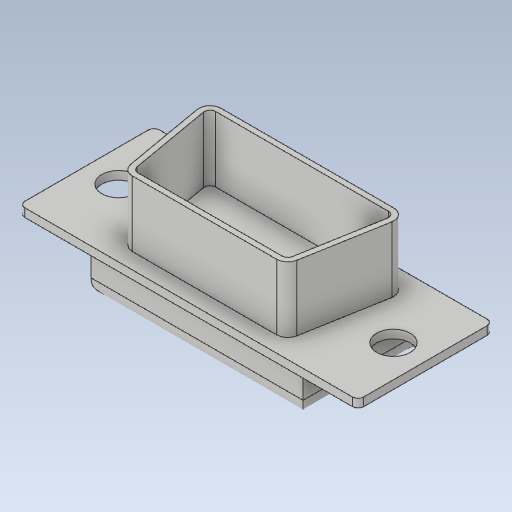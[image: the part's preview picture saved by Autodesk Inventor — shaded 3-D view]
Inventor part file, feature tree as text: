
AUTODESK INVENTOR PART (.ipt)
format: ipt  version: 2020 (Build 240168000, 168)  size: 221,184 bytes
history: native  units: in
note: dims shown in document units (in); Inventor stores cm internally (conversion verified against a paired STEP export)
features: sketch x5, projected_geometry x4, extrude x3, fillet x2, hole x1
ambient origin geometry x8: Origin, YZ Plane, XZ Plane, XY Plane, X Axis, Y Axis, Z Axis, Center Point
bodies: Solid1 (feature_tree)
feature tree (15):
  extrude  "Extrusion1"  Depth=0.4823in
  fillet  "Fillet1"  Radius=0.0299in
  hole  "Hole1"  [1 undecoded]
  extrude  "Extrusion2"  Depth=0.6871in
  extrude  "Extrusion3"  Depth=0.6661in
  fillet  "Fillet2"  Radius=0.0197in
  sketch  "Sketch5"  dims[d18=0.0197in d19=0.2343in d20=0.0in d21=0.7591in d22=0.422in d23=0.1579in d24=0.0in d25=0.0591in]
  sketch  "Sketch1"  dims[d0=1.213in d1=0.4823in d2=0.0299in d3=0.0in]
  sketch  "Sketch2"  dims[d4=0.0197in d5=0.9839in]
  projected_geometry  "Projected Loop1"
  sketch  "Sketch3"  dims[d6=0.1201in d7=0.2362in d8=0.1575in d9=0.0787in d10=90.0deg d11=0.315in d12=0.8108in d14=0.6871in]
  projected_geometry  "Projected Loop2"
  sketch  "Sketch4"  dims[d15=0.3291in d16=0.6661in d17=0.0197in]
  projected_geometry  "Projected Loop3"
  projected_geometry  "Projected Loop4"
note: 1 required parameter value undecoded (feature->parameter linkage not recoverable at this tier; creation-order binding heuristic only, values carry confidence <= 0.55)
